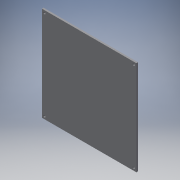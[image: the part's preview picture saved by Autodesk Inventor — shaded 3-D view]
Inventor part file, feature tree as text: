
AUTODESK INVENTOR PART (.ipt)
format: ipt  version: 2018 (Build 220112000, 112)  size: 109,056 bytes
history: native  units: in
note: dims shown in document units (in); Inventor stores cm internally (conversion verified against a paired STEP export)
features: extrude x2, sketch x2, chamfer x1, projected_geometry x1
ambient origin geometry x8: Origin, YZ Plane, XZ Plane, XY Plane, X Axis, Y Axis, Z Axis, Center Point
bodies: Solid1 (feature_tree)
feature tree (6):
  extrude  "Extrusion1"  Depth=8.6614in
  extrude  "Extrusion2"  Depth=0.0787in
  chamfer  "Chamfer1"  Distance=0.2362in
  sketch  "Sketch1"  dims[d0=8.6614in d1=8.6614in]
  sketch  "Sketch2"  dims[d2=0.1575in d3=0.0in d4=0.2362in d5=0.2362in d6=0.1181in d7=1.5748in d9=360.0deg d11=0.1575in d12=0.0in d13=0.0394in d14=0.0787in d15=45.0deg]
  projected_geometry  "Projected Loop1"
